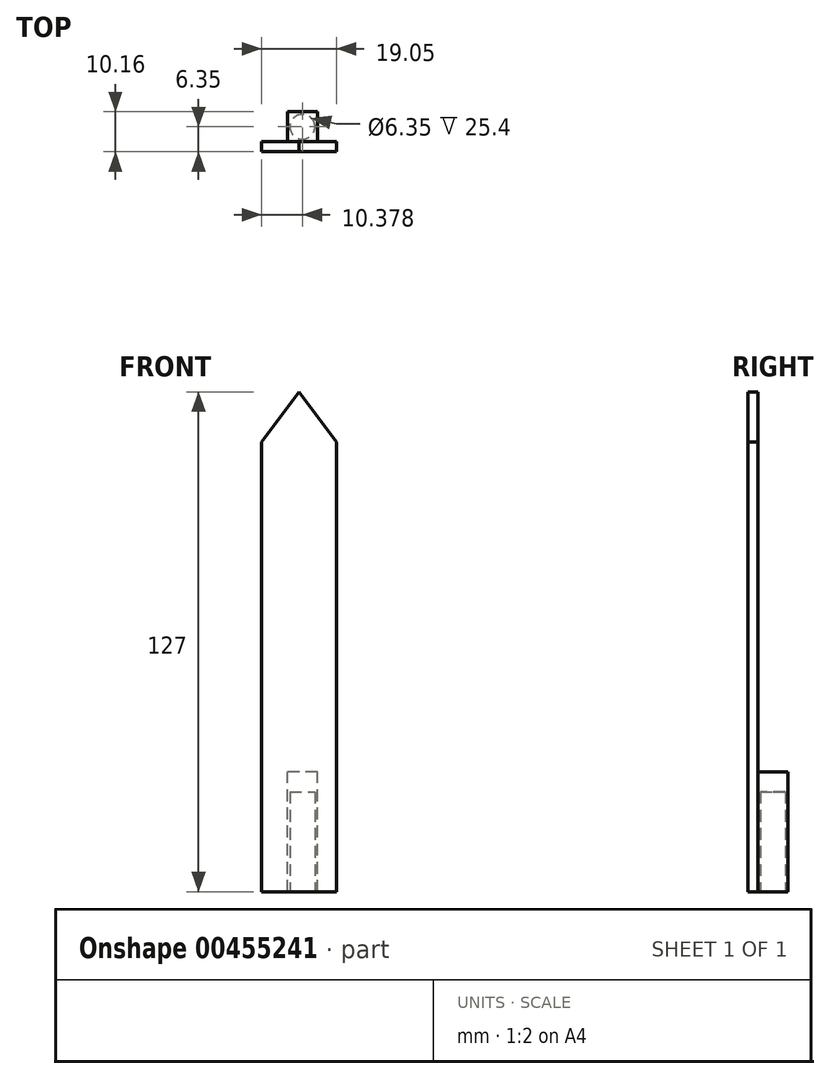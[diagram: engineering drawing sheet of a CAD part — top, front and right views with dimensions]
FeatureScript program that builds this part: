
annotation { "Feature Type Name" : "Feature", "Feature Type Description" : "" }
export const myFeature = defineFeature(function(context is Context, id is Id, definition is map)
    precondition{}
    {
        {
            var Q0;
            Q0=qCreatedBy(makeId("Front.planeOp"),FACE);
            var sketch = newSketch(context, id + "F0", { "sketchPlane" : qUnion([Q0])});
            skLineSegment(sketch, "E0", {"start": v(0, 0) * mm, "end": v(19.05, 0) * mm});
            skLineSegment(sketch, "E1", {"start": v(19.05, 0) * mm, "end": v(19.05, 114.3) * mm});
            skLineSegment(sketch, "E2", {"start": v(19.05, 114.3) * mm, "end": v(9.52, 127) * mm});
            skPoint(sketch, "E2.endSnap0", {"position": v(9.53, 0) * mm});
            skLineSegment(sketch, "E3", {"start": v(9.52, 127) * mm, "end": v(0, 114.3) * mm});
            skLineSegment(sketch, "E4", {"start": v(0, 114.3) * mm, "end": v(0, 0) * mm});
            skSolve(sketch);
        }
        {
            var Q0;
            Q0 = qSketchRegion(id + "F0", true);
            extrude(context, id + "F1", {"entities" : qUnion([Q0]), "depth" : 2.54 * mm});
        }
        {
            var Q0;
            Q0=makeQuery(id+"F1.opExtrude","CAP_FACE",FACE,{"disambiguationData":[OSD([sQuery(id+"F0.wireOp",EDGE,"E0"),sQuery(id+"F0.wireOp",EDGE,"E1"),sQuery(id+"F0.wireOp",EDGE,"E2"),sQuery(id+"F0.wireOp",EDGE,"E3"),sQuery(id+"F0.wireOp",EDGE,"E4")])],"isStart":true});
            var sketch = newSketch(context, id + "F2", { "sketchPlane" : qUnion([Q0])});
            skLineSegment(sketch, "E5.bottom", {"start": v(-14.19, 0) * mm, "end": v(-6.57, 0) * mm});
            skLineSegment(sketch, "E5.top", {"start": v(-14.19, 30.48) * mm, "end": v(-6.57, 30.48) * mm});
            skLineSegment(sketch, "E5.left", {"start": v(-14.19, 0) * mm, "end": v(-14.19, 30.48) * mm});
            skLineSegment(sketch, "E5.right", {"start": v(-6.57, 0) * mm, "end": v(-6.57, 30.48) * mm});
            skSolve(sketch);
        }
        {
            var Q0;
            Q0 = qSketchRegion(id + "F2", true);
            extrude(context, id + "F3", {"entities" : qUnion([Q0]), "operationType" : NewBodyOperationType.ADD, "depth" : 7.62 * mm});
        }
        {
            var Q0;
            Q0=makeQuery(id+"F3.boolean.opBoolean","MERGE",FACE,{"derivedFrom":[makeQuery(id+"F1.opExtrude","SWEPT_FACE",FACE,{"disambiguationData":[OSD([sQuery(id+"F0.wireOp",EDGE,"E0")])]}),makeQuery(id+"F3.opExtrude","SWEPT_FACE",FACE,{"disambiguationData":[OSD([sQuery(id+"F2.wireOp",EDGE,"E5.bottom")])]})]});
            var sketch = newSketch(context, id + "F4", { "sketchPlane" : qUnion([Q0])});
            skCircle(sketch, "E6", {"center": v(10.38, -3.81) * mm, "radius": 3.18 * mm});
            skPoint(sketch, "E6.centerSnap0", {"position": v(14.19, -3.81) * mm});
            skPoint(sketch, "E6.centerSnap1", {"position": v(10.38, -7.62) * mm});
            skSolve(sketch);
        }
        {
            var Q0;
            Q0 = qSketchRegion(id + "F4", true);
            extrude(context, id + "F5", {"entities" : qUnion([Q0]), "operationType" : NewBodyOperationType.REMOVE, "oppositeDirection" : true, "depth" : 25.4 * mm});
        }
    });
